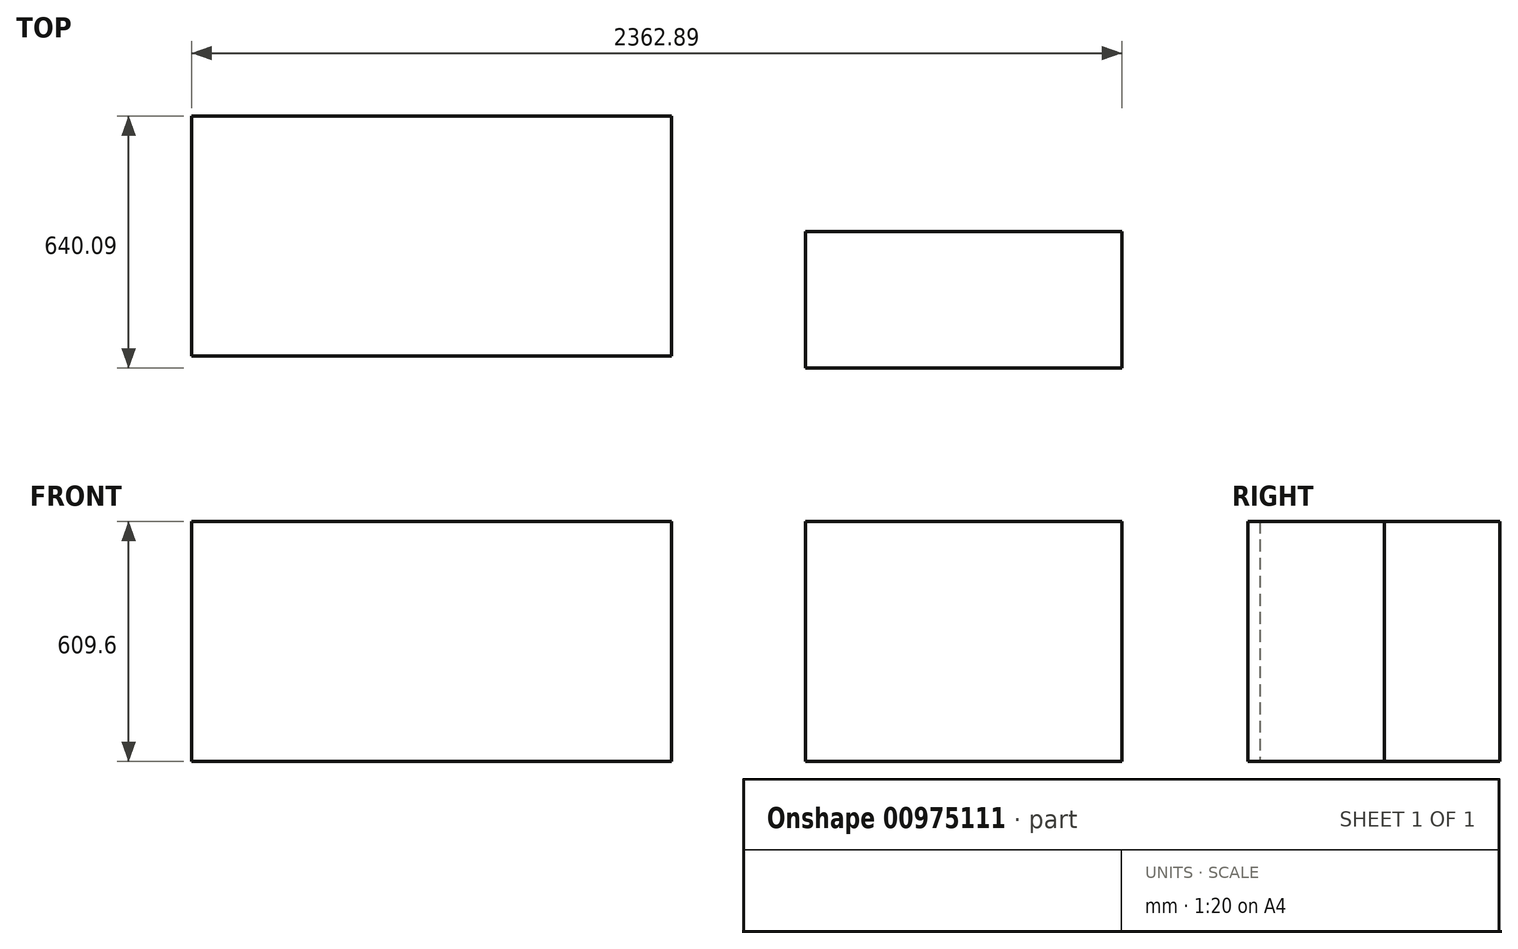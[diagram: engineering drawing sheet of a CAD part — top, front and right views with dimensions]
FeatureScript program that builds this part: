
annotation { "Feature Type Name" : "Feature", "Feature Type Description" : "" }
export const myFeature = defineFeature(function(context is Context, id is Id, definition is map)
    precondition{}
    {
        {
            var Q0;
            Q0=qCreatedBy(makeId("Top.planeOp"),FACE);
            var sketch = newSketch(context, id + "F0", { "sketchPlane" : qUnion([Q0])});
            skLineSegment(sketch, "E0.bottom", {"start": v(-540.52, 292.8) * mm, "end": v(678.68, 292.8) * mm});
            skLineSegment(sketch, "E0.top", {"start": v(-540.52, -316.8) * mm, "end": v(678.68, -316.8) * mm});
            skLineSegment(sketch, "E0.left", {"start": v(-540.52, 292.8) * mm, "end": v(-540.52, -316.8) * mm});
            skLineSegment(sketch, "E0.right", {"start": v(678.68, 292.8) * mm, "end": v(678.68, -316.8) * mm});
            skLineSegment(sketch, "E1.bottom", {"start": v(1018.8, 0) * mm, "end": v(1822.37, 0) * mm});
            skLineSegment(sketch, "E1.top", {"start": v(1018.8, -347.29) * mm, "end": v(1822.37, -347.29) * mm});
            skLineSegment(sketch, "E1.left", {"start": v(1018.8, 0) * mm, "end": v(1018.8, -347.29) * mm});
            skLineSegment(sketch, "E1.right", {"start": v(1822.37, 0) * mm, "end": v(1822.37, -347.29) * mm});
            skSolve(sketch);
        }
        {
            var Q0;
            Q0=makeQuery(id+"F0.imprint","IMPRINT",FACE,{"disambiguationData":[TD([[makeQuery(id+"F0.imprint","IMPRINT",EDGE,{"derivedFrom":sQuery(id+"F0.wireOp",EDGE,"E0.bottom")}),-1.0]])]});
            var Q1;
            Q1=makeQuery(id+"F0.imprint","IMPRINT",FACE,{"disambiguationData":[TD([[makeQuery(id+"F0.imprint","IMPRINT",EDGE,{"derivedFrom":sQuery(id+"F0.wireOp",EDGE,"E1.bottom")}),-1.0]])]});
            extrude(context, id + "F1", {"entities" : qUnion([Q0, Q1]), "depth" : 609.6 * mm, "offsetDistance" : 25.4 * mm});
        }
        {
            var Q0;
            Q0=makeQuery(id+"F1.opExtrude","CAP_FACE",FACE,{"disambiguationData":[OSD([sQuery(id+"F0.wireOp",EDGE,"E0.bottom"),sQuery(id+"F0.wireOp",EDGE,"E0.top"),sQuery(id+"F0.wireOp",EDGE,"E0.left"),sQuery(id+"F0.wireOp",EDGE,"E0.right")])],"isStart":false});
            var sketch = newSketch(context, id + "F2", { "sketchPlane" : qUnion([Q0])});
            skLineSegment(sketch, "E2", {"start": v(69.08, 292.8) * mm, "end": v(69.08, 618.69) * mm});
            skLineSegment(sketch, "E3", {"start": v(1383.17, 0) * mm, "end": v(1383.17, 850.29) * mm});
            skLineSegment(sketch, "E4", {"start": v(1383.17, 850.29) * mm, "end": v(-2458.66, 850.29) * mm});
            skLineSegment(sketch, "E5", {"start": v(-2458.66, 850.29) * mm, "end": v(-2458.66, 2335.25) * mm});
            skLineSegment(sketch, "E6", {"start": v(69.08, 618.69) * mm, "end": v(1383.17, 618.69) * mm});
            skLineSegment(sketch, "E7", {"start": v(-81.36, 292.8) * mm, "end": v(-81.36, 754.92) * mm});
            skLineSegment(sketch, "E8", {"start": v(-81.36, 754.92) * mm, "end": v(-2581.27, 754.92) * mm});
            skLineSegment(sketch, "E9", {"start": v(-2581.27, 754.92) * mm, "end": v(-2581.27, 2335.25) * mm});
            skSolve(sketch);
        }
        {
            var Q0;
            Q0=makeQuery(id+"F2.imprint","IMPRINT",FACE,{"disambiguationData":[TD([[makeQuery(id+"F2.imprint","IMPRINT",EDGE,{"derivedFrom":makeQuery(id+"F1.opExtrude","CAP_EDGE",EDGE,{"disambiguationData":[OSD([sQuery(id+"F0.wireOp",EDGE,"E0.top")])],"isStart":false})}),1.0]])]});
            var sketch = newSketch(context, id + "F3", { "sketchPlane" : qUnion([Q0])});
            skCircle(sketch, "E10", {"center": v(-898.77, 3697.6) * mm, "radius": 116 * mm});
            skSolve(sketch);
        }
        {
            var Q0;
            Q0=sQuery(id+"F3.wireOp",EDGE,"E10");
            extrude(context, id + "F4", {"bodyType" : ToolBodyType.SURFACE, "surfaceEntities" : qUnion([Q0]), "depth" : 25.4 * mm, "offsetDistance" : 25.4 * mm});
        }
    });
